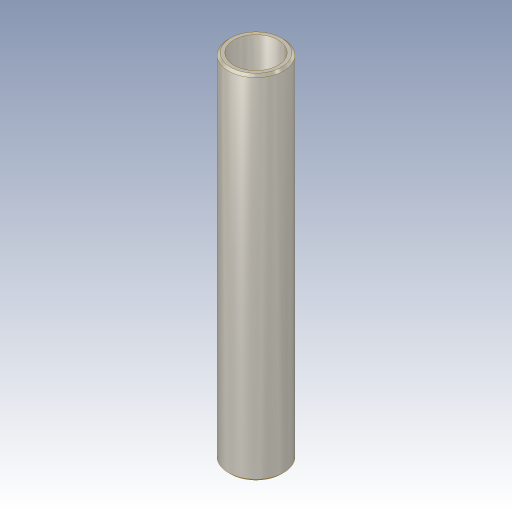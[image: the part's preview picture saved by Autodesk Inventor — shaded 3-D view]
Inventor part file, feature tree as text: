
AUTODESK INVENTOR PART (.ipt)
format: ipt  version: 2023.3 (Build 273359000, 359)  size: 133,632 bytes
history: native  units: in
note: dims shown in document units (in); Inventor stores cm internally (conversion verified against a paired STEP export)
features: revolve x1, chamfer x1, sketch x1
ambient origin geometry x8: Origin, YZ Plane, XZ Plane, XY Plane, X Axis, Y Axis, Z Axis, Center Point
bodies: Body1 (feature_tree)
feature tree (3):
  revolve  "Umdrehung1"
  chamfer  "Fase1"  Distance=0.6299in
  sketch  "Skizze3"  dims[d4=0.0984in d5=0.6299in d6=0.0787in d7=90.0deg d8=0.0039in d9=0.0787in d10=45.0deg]
